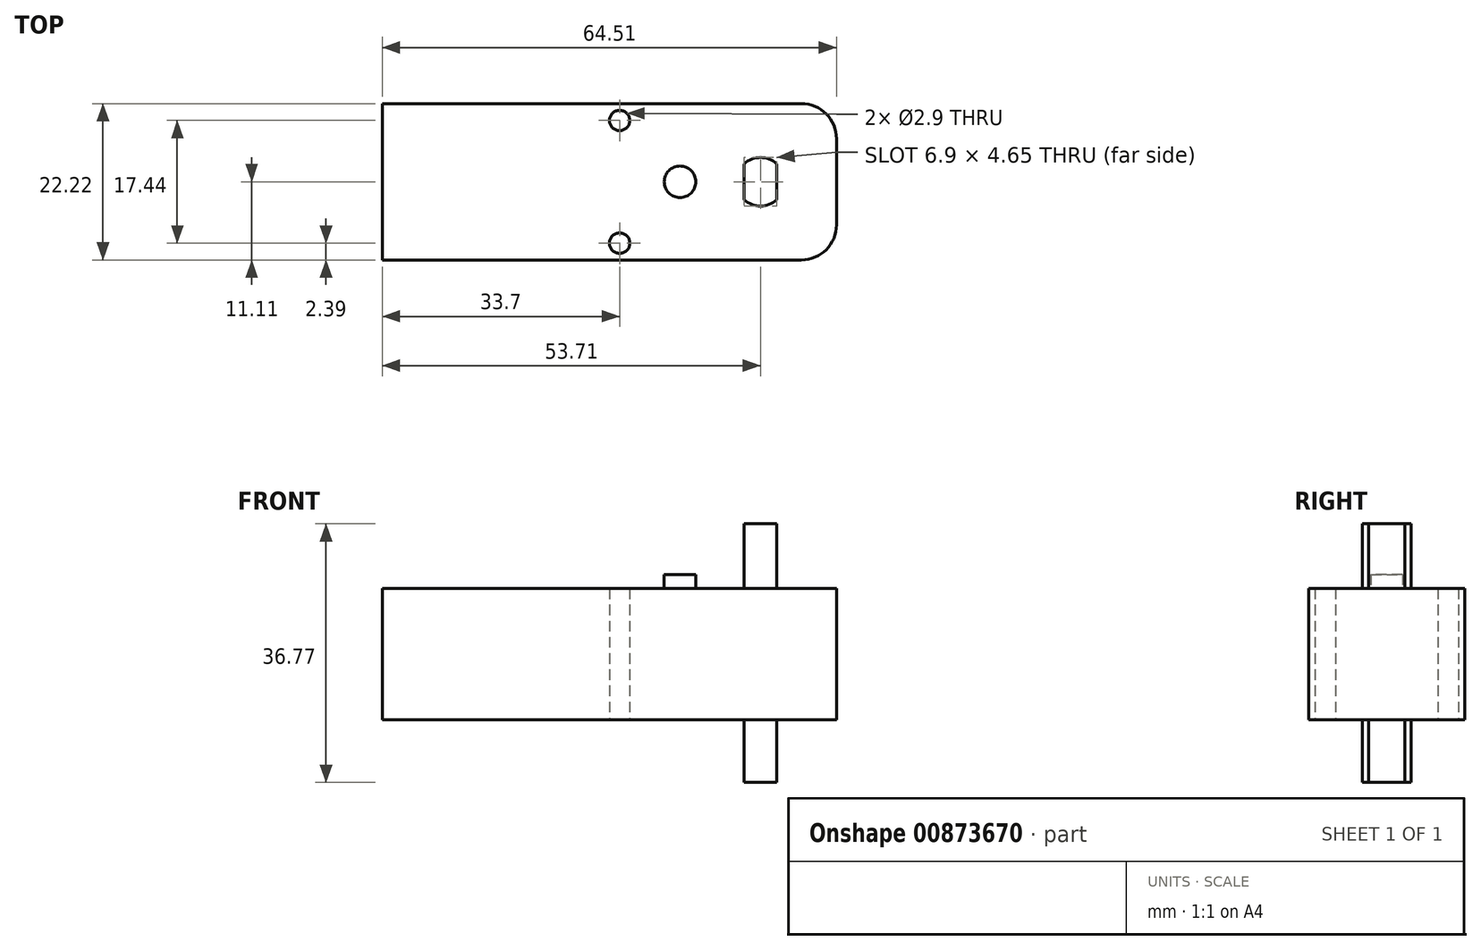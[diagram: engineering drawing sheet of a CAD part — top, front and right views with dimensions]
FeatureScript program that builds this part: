
annotation { "Feature Type Name" : "Feature", "Feature Type Description" : "" }
export const myFeature = defineFeature(function(context is Context, id is Id, definition is map)
    precondition{}
    {
        {
            var Q0;
            Q0=qCreatedBy(makeId("Top.planeOp"),FACE);
            var sketch = newSketch(context, id + "F0", { "sketchPlane" : qUnion([Q0])});
            skCircle(sketch, "E0", {"center": v(0, 0) * mm, "radius": 4.87 * mm});
            skCircle(sketch, "E1", {"center": v(-20.01, 8.72) * mm, "radius": 1.45 * mm});
            skCircle(sketch, "E2.MirrorC", {"center": v(-20.01, -8.72) * mm, "radius": 1.45 * mm});
            skLineSegment(sketch, "E3.bottom", {"start": v(5.8, -11.1) * mm, "end": v(-53.7, -11.11) * mm});
            skLineSegment(sketch, "E3.top", {"start": v(5.8, 11.1) * mm, "end": v(-53.71, 11.1) * mm});
            skLineSegment(sketch, "E3.left", {"start": v(10.8, -6.1) * mm, "end": v(10.8, 6.11) * mm});
            skLineSegment(sketch, "E3.right", {"start": v(-53.71, -11.11) * mm, "end": v(-53.71, 11.1) * mm});
            skPoint(sketch, "E3.middle", {"position": v(-21.46, 0) * mm});
            skCircle(sketch, "E4", {"center": v(-11.43, 0) * mm, "radius": 2.24 * mm});
            skPoint(sketch, "E5.visualSharp", {"position": v(10.8, 11.11) * mm});
            skArc(sketch, "E5.filletArc", {"start": v(10.8, 6.11) * mm, "mid": v(9.34, 9.65) * mm, "end": v(5.8, 11.1) * mm});
            skPoint(sketch, "E6.visualSharp", {"position": v(10.8, -11.1) * mm});
            skArc(sketch, "E6.filletArc", {"start": v(5.8, -11.1) * mm, "mid": v(9.34, -9.65) * mm, "end": v(10.8, -6.1) * mm});
            skCircle(sketch, "E7", {"center": v(0, 0) * mm, "radius": 3.42 * mm});
            skSolve(sketch);
        }
        {
            var Q0;
            Q0=makeQuery(id+"F0.imprint","IMPRINT",FACE,{"disambiguationData":[TD([[makeQuery(id+"F0.imprint","IMPRINT",EDGE,{"derivedFrom":sQuery(id+"F0.wireOp",EDGE,"E0")}),-1.0]])]});
            var Q1;
            Q1=makeQuery(id+"F0.imprint","IMPRINT",FACE,{"disambiguationData":[TD([[makeQuery(id+"F0.imprint","IMPRINT",EDGE,{"derivedFrom":sQuery(id+"F0.wireOp",EDGE,"E4")}),1.0]])]});
            var Q2;
            Q2=makeQuery(id+"F0.imprint","IMPRINT",FACE,{"disambiguationData":[TD([[makeQuery(id+"F0.imprint","IMPRINT",EDGE,{"derivedFrom":sQuery(id+"F0.wireOp",EDGE,"E7")}),1.0]])]});
            var Q3;
            Q3=makeQuery(id+"F0.imprint","IMPRINT",FACE,{"disambiguationData":[TD([[makeQuery(id+"F0.imprint","IMPRINT",EDGE,{"derivedFrom":sQuery(id+"F0.wireOp",EDGE,"E0")}),1.0]])]});
            extrude(context, id + "F1", {"entities" : qUnion([Q0, Q1, Q2, Q3]), "depth" : 18.64 * mm, "offsetDistance" : 25 * mm});
        }
        {
            var Q0;
            Q0=makeQuery(id+"F1.opExtrude","CAP_FACE",FACE,{"disambiguationData":[OSD([sQuery(id+"F0.wireOp",EDGE,"E1"),sQuery(id+"F0.wireOp",EDGE,"E2.MirrorC"),sQuery(id+"F0.wireOp",EDGE,"E3.bottom"),sQuery(id+"F0.wireOp",EDGE,"E3.top"),sQuery(id+"F0.wireOp",EDGE,"E3.left"),sQuery(id+"F0.wireOp",EDGE,"E3.right"),sQuery(id+"F0.wireOp",EDGE,"E5.filletArc"),sQuery(id+"F0.wireOp",EDGE,"E6.filletArc")])],"isStart":false});
            var sketch = newSketch(context, id + "F2", { "sketchPlane" : qUnion([Q0])});
            skArc(sketch, "E8", {"start": v(-2.33, -2.55) * mm, "mid": v(0, -3.45) * mm, "end": v(2.33, -2.55) * mm});
            skLineSegment(sketch, "E9.top", {"start": v(2.32, 2.55) * mm, "end": v(-2.33, 2.55) * mm});
            skLineSegment(sketch, "E9.left", {"start": v(2.33, -2.55) * mm, "end": v(2.33, 2.55) * mm});
            skLineSegment(sketch, "E9.right", {"start": v(-2.33, -2.55) * mm, "end": v(-2.33, 2.55) * mm});
            skArc(sketch, "E10.trimOffspring", {"start": v(2.33, 2.55) * mm, "mid": v(0, 3.45) * mm, "end": v(-2.33, 2.55) * mm});
            skSolve(sketch);
        }
        {
            var Q0;
            Q0=qSketchRegion(id+"F2",true);
            extrude(context, id + "F3", {"entities" : qUnion([Q0]), "operationType" : NewBodyOperationType.ADD, "depth" : 9.2 * mm, "offsetDistance" : 25 * mm});
        }
        {
            var Q0;
            Q0=makeQuery(id+"F1.opExtrude","CAP_FACE",FACE,{"disambiguationData":[OSD([sQuery(id+"F0.wireOp",EDGE,"E1"),sQuery(id+"F0.wireOp",EDGE,"E2.MirrorC"),sQuery(id+"F0.wireOp",EDGE,"E3.bottom"),sQuery(id+"F0.wireOp",EDGE,"E3.top"),sQuery(id+"F0.wireOp",EDGE,"E3.left"),sQuery(id+"F0.wireOp",EDGE,"E3.right"),sQuery(id+"F0.wireOp",EDGE,"E5.filletArc"),sQuery(id+"F0.wireOp",EDGE,"E6.filletArc")])],"isStart":false});
            var sketch = newSketch(context, id + "F4", { "sketchPlane" : qUnion([Q0])});
            skCircle(sketch, "E11", {"center": v(-11.43, 0) * mm, "radius": 2.24 * mm});
            skSolve(sketch);
        }
        {
            var Q0;
            Q0=qSketchRegion(id+"F4",true);
            extrude(context, id + "F5", {"entities" : qUnion([Q0]), "operationType" : NewBodyOperationType.ADD, "depth" : 2 * mm, "offsetDistance" : 25 * mm});
        }
        {
            var Q0;
            Q0=makeQuery(id+"F0.imprint","IMPRINT",FACE,{"disambiguationData":[TD([[makeQuery(id+"F0.imprint","IMPRINT",EDGE,{"derivedFrom":sQuery(id+"F0.wireOp",EDGE,"E0")}),-1.0]])]});
            var sketch = newSketch(context, id + "F6", { "sketchPlane" : qUnion([Q0])});
            skCircle(sketch, "E12", {"center": v(0, 0) * mm, "radius": 3.45 * mm});
            skLineSegment(sketch, "E13.bottom", {"start": v(-2.33, -2.55) * mm, "end": v(2.33, -2.55) * mm});
            skLineSegment(sketch, "E13.top", {"start": v(-2.33, 2.55) * mm, "end": v(2.33, 2.55) * mm});
            skLineSegment(sketch, "E13.left", {"start": v(-2.33, -2.55) * mm, "end": v(-2.33, 2.55) * mm});
            skLineSegment(sketch, "E13.right", {"start": v(2.33, -2.55) * mm, "end": v(2.33, 2.55) * mm});
            skSolve(sketch);
        }
        {
            var Q0;
            {var subQ0=sQuery(id+"F6.wireOp",EDGE,"E13.top");Q0=makeQuery(id+"F6.imprint","IMPRINT",FACE,{"disambiguationData":[TD([[makeQuery(id+"F6.imprint","IMPRINT",EDGE,{"derivedFrom":subQ0}),1.0]])]});}
            var Q1;
            {var subQ0=sQuery(id+"F6.wireOp",EDGE,"E13.bottom");Q1=makeQuery(id+"F6.imprint","IMPRINT",FACE,{"disambiguationData":[TD([[makeQuery(id+"F6.imprint","IMPRINT",EDGE,{"derivedFrom":subQ0}),-1.0]])]});}
            var Q2;
            Q2=makeQuery(id+"F6.imprint","IMPRINT",FACE,{"disambiguationData":[TD([[makeQuery(id+"F6.imprint","IMPRINT",EDGE,{"derivedFrom":sQuery(id+"F6.wireOp",EDGE,"E13.bottom")}),1.0]])]});
            extrude(context, id + "F7", {"entities" : qUnion([Q0, Q1, Q2]), "operationType" : NewBodyOperationType.ADD, "oppositeDirection" : true, "depth" : 8.93 * mm, "offsetDistance" : 25 * mm});
        }
    });
